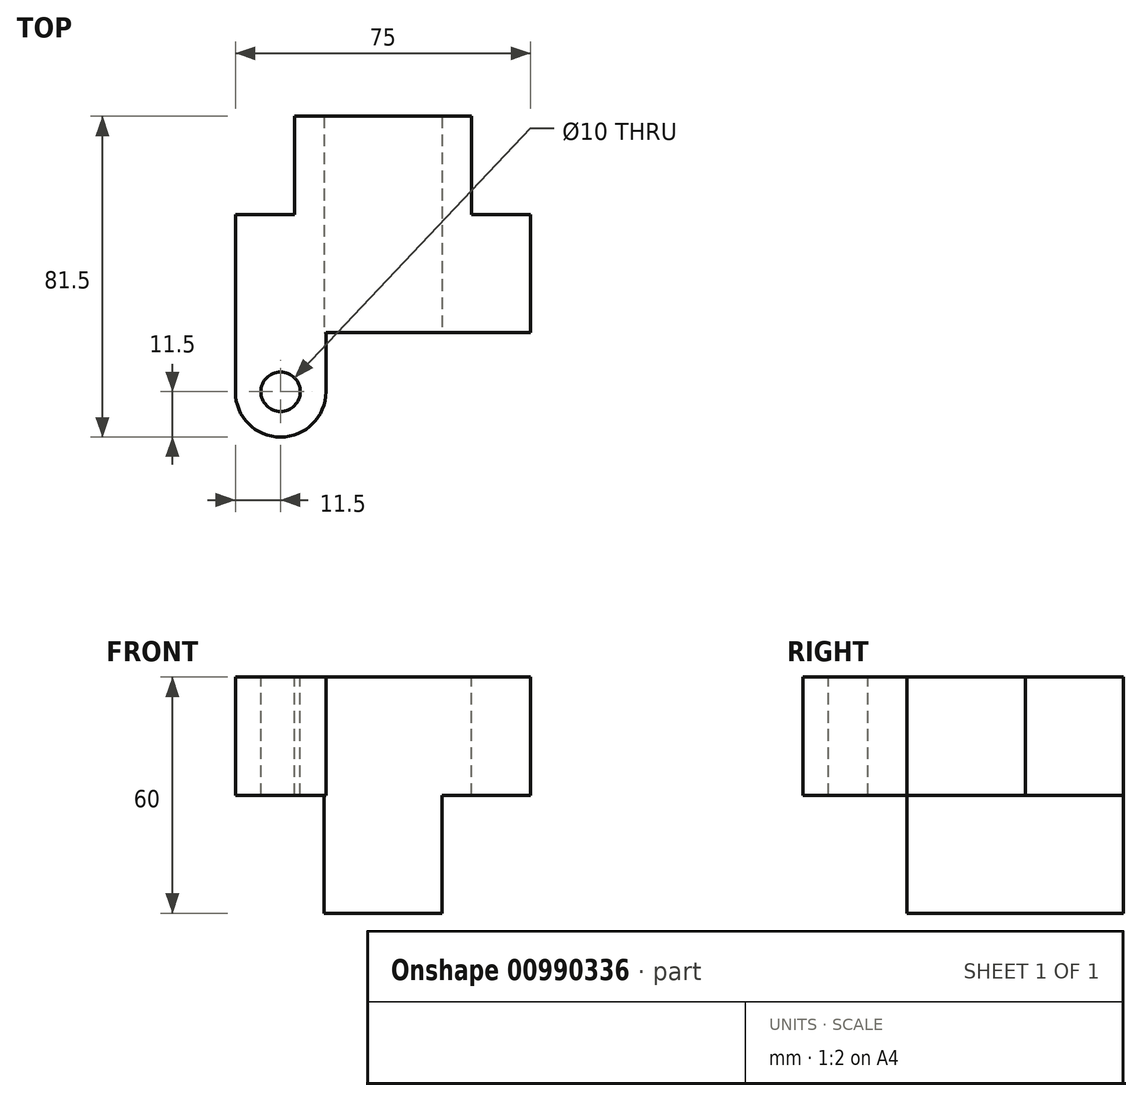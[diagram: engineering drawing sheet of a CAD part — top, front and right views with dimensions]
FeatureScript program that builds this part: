
annotation { "Feature Type Name" : "Feature", "Feature Type Description" : "" }
export const myFeature = defineFeature(function(context is Context, id is Id, definition is map)
    precondition{}
    {
        {
            var Q0;
            Q0=qCreatedBy(makeId("Front.planeOp"),FACE);
            var sketch = newSketch(context, id + "F0", { "sketchPlane" : qUnion([Q0])});
            skLineSegment(sketch, "E0", {"start": v(0, 30) * mm, "end": v(-37.5, 30) * mm});
            skLineSegment(sketch, "E1", {"start": v(-37.5, 30) * mm, "end": v(-37.5, 0) * mm});
            skLineSegment(sketch, "E2", {"start": v(-37.5, 0) * mm, "end": v(-15, 0) * mm});
            skLineSegment(sketch, "E3", {"start": v(-15, 0) * mm, "end": v(-15, -30) * mm});
            skLineSegment(sketch, "E4", {"start": v(-15, -30) * mm, "end": v(0, -30) * mm});
            skLineSegment(sketch, "E5.MirrorCS", {"start": v(37.5, 0) * mm, "end": v(15, 0) * mm});
            skLineSegment(sketch, "E6.MirrorCS", {"start": v(15, -30) * mm, "end": v(0, -30) * mm});
            skLineSegment(sketch, "E7.MirrorCS", {"start": v(37.5, 30) * mm, "end": v(37.5, 0) * mm});
            skLineSegment(sketch, "E8.MirrorCS", {"start": v(0, 30) * mm, "end": v(37.5, 30) * mm});
            skLineSegment(sketch, "E9.MirrorCS", {"start": v(15, 0) * mm, "end": v(15, -30) * mm});
            skSolve(sketch);
        }
        {
            var Q0;
            Q0=makeQuery(id+"F0.imprint","IMPRINT",FACE,{"disambiguationData":[TD([[makeQuery(id+"F0.imprint","IMPRINT",EDGE,{"derivedFrom":sQuery(id+"F0.wireOp",EDGE,"E0")}),1.0]])]});
            extrude(context, id + "F1", {"entities" : qUnion([Q0]), "oppositeDirection" : true, "depth" : 55 * mm, "offsetDistance" : 25 * mm});
        }
        {
            var Q0;
            Q0=makeQuery(id+"F1.opExtrude","SWEPT_FACE",FACE,{"disambiguationData":[OSD([sQuery(id+"F0.wireOp",EDGE,"E0"),sQuery(id+"F0.wireOp",EDGE,"E8.MirrorCS")])]});
            var sketch = newSketch(context, id + "F2", { "sketchPlane" : qUnion([Q0])});
            skLineSegment(sketch, "E10", {"start": v(0, 55) * mm, "end": v(-22.5, 55) * mm});
            skPoint(sketch, "E10.startSnap0", {"position": v(0, 55) * mm});
            skLineSegment(sketch, "E11", {"start": v(-22.5, 55) * mm, "end": v(-22.5, 30) * mm});
            skLineSegment(sketch, "E12", {"start": v(-22.5, 30) * mm, "end": v(-37.5, 30) * mm});
            skLineSegment(sketch, "E13", {"start": v(-37.5, 30) * mm, "end": v(-37.5, 0) * mm});
            skLineSegment(sketch, "E14", {"start": v(-37.5, 0) * mm, "end": v(0, 0) * mm});
            skLineSegment(sketch, "E15.MirrorCS", {"start": v(37.5, 0) * mm, "end": v(0, 0) * mm});
            skLineSegment(sketch, "E16.MirrorCS", {"start": v(37.5, 30) * mm, "end": v(37.5, 0) * mm});
            skLineSegment(sketch, "E17.MirrorCS", {"start": v(22.5, 30) * mm, "end": v(37.5, 30) * mm});
            skLineSegment(sketch, "E18.MirrorCS", {"start": v(0, 55) * mm, "end": v(22.5, 55) * mm});
            skLineSegment(sketch, "E19.MirrorCS", {"start": v(22.5, 55) * mm, "end": v(22.5, 30) * mm});
            skSolve(sketch);
        }
        {
            var Q0;
            {var subQ0=sQuery(id+"F2.wireOp",EDGE,"E17.MirrorCS");Q0=makeQuery(id+"F2.imprint","IMPRINT",FACE,{"disambiguationData":[TD([[makeQuery(id+"F2.imprint","IMPRINT",EDGE,{"derivedFrom":subQ0}),1.0]])]});}
            var Q1;
            {var subQ0=sQuery(id+"F2.wireOp",EDGE,"E11");Q1=makeQuery(id+"F2.imprint","IMPRINT",FACE,{"disambiguationData":[TD([[makeQuery(id+"F2.imprint","IMPRINT",EDGE,{"derivedFrom":subQ0}),-1.0]])]});}
            extrude(context, id + "F3", {"entities" : qUnion([Q0, Q1]), "operationType" : NewBodyOperationType.REMOVE, "oppositeDirection" : true, "depth" : 62 * mm, "offsetDistance" : 25 * mm});
        }
        {
            var Q0;
            Q0=makeQuery(id+"F1.opExtrude","SWEPT_FACE",FACE,{"disambiguationData":[OSD([sQuery(id+"F0.wireOp",EDGE,"E0"),sQuery(id+"F0.wireOp",EDGE,"E8.MirrorCS")])]});
            var sketch = newSketch(context, id + "F4", { "sketchPlane" : qUnion([Q0])});
            skArc(sketch, "E20", {"start": v(-37.5, -15) * mm, "mid": v(-26, -26.5) * mm, "end": v(-14.5, -15) * mm});
            skCircle(sketch, "E21", {"center": v(-26, -15) * mm, "radius": 5 * mm});
            skLineSegment(sketch, "E22", {"start": v(-37.5, -15) * mm, "end": v(-37.5, 0) * mm});
            skLineSegment(sketch, "E23", {"start": v(-37.5, 0) * mm, "end": v(-14.5, 0) * mm});
            skLineSegment(sketch, "E24", {"start": v(-14.5, 0) * mm, "end": v(-14.5, -15) * mm});
            skArc(sketch, "E25.MirrorCS", {"start": v(37.5, -15) * mm, "mid": v(26, -26.5) * mm, "end": v(14.5, -15) * mm});
            skLineSegment(sketch, "E26.MirrorCS", {"start": v(14.5, 0) * mm, "end": v(14.5, -15) * mm});
            skLineSegment(sketch, "E27.MirrorCS", {"start": v(37.5, 0) * mm, "end": v(14.5, 0) * mm});
            skLineSegment(sketch, "E28.MirrorCS", {"start": v(37.5, -15) * mm, "end": v(37.5, 0) * mm});
            skCircle(sketch, "E29.MirrorC", {"center": v(26, -15) * mm, "radius": 5 * mm});
            skSolve(sketch);
        }
        {
            var Q0;
            Q0=makeQuery(id+"F4.imprint","IMPRINT",FACE,{"disambiguationData":[TD([[makeQuery(id+"F4.imprint","IMPRINT",EDGE,{"derivedFrom":sQuery(id+"F4.wireOp",EDGE,"E20")}),1.0]])]});
            var Q1;
            Q1=makeQuery(id+"F4.imprint","IMPRINT",FACE,{"disambiguationData":[TD([[makeQuery(id+"F4.imprint","IMPRINT",EDGE,{"derivedFrom":sQuery(id+"F4.wireOp",EDGE,"E25.MirrorCS")}),-1.0]])]});
            extrude(context, id + "F5", {"entities" : qUnion([Q0, Q1]), "operationType" : NewBodyOperationType.ADD, "oppositeDirection" : true, "depth" : 30 * mm, "offsetDistance" : 25 * mm});
        }
    });
